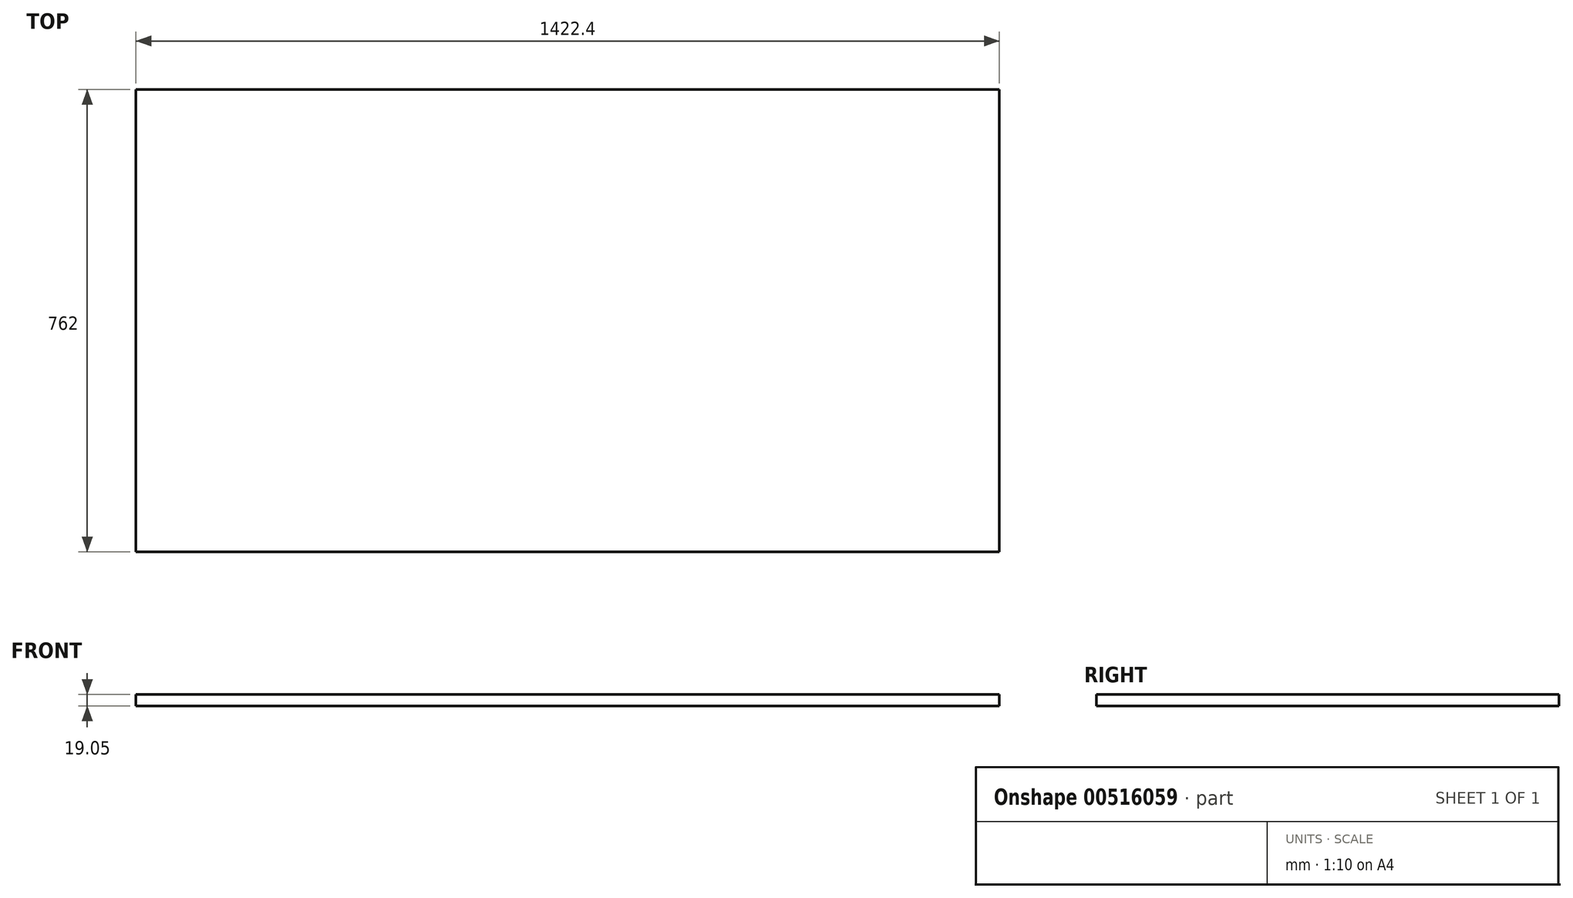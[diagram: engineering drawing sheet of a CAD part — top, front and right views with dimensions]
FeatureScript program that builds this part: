
annotation { "Feature Type Name" : "Feature", "Feature Type Description" : "" }
export const myFeature = defineFeature(function(context is Context, id is Id, definition is map)
    precondition{}
    {
        {
            var Q0;
            Q0=qCreatedBy(makeId("Top.planeOp"),FACE);
            var sketch = newSketch(context, id + "F0", { "sketchPlane" : qUnion([Q0])});
            skLineSegment(sketch, "E0.bottom", {"start": v(711.2, -381) * mm, "end": v(-711.2, -381) * mm});
            skLineSegment(sketch, "E0.top", {"start": v(711.2, 381) * mm, "end": v(-711.2, 381) * mm});
            skLineSegment(sketch, "E0.left", {"start": v(711.2, -381) * mm, "end": v(711.2, 381) * mm});
            skLineSegment(sketch, "E0.right", {"start": v(-711.2, -381) * mm, "end": v(-711.2, 381) * mm});
            skPoint(sketch, "E0.middle", {"position": v(0, 0) * mm});
            skLineSegment(sketch, "E1.bottom", {"start": v(-711.2, -381) * mm, "end": v(1727.2, -381) * mm, "construction": true});
            skLineSegment(sketch, "E1.top", {"start": v(-711.2, 838.2) * mm, "end": v(1727.2, 838.2) * mm, "construction": true});
            skLineSegment(sketch, "E1.left", {"start": v(-711.2, -381) * mm, "end": v(-711.2, 838.2) * mm, "construction": true});
            skLineSegment(sketch, "E1.right", {"start": v(1727.2, -381) * mm, "end": v(1727.2, 838.2) * mm, "construction": true});
            skLineSegment(sketch, "E2.bottom", {"start": v(-711.2, 381) * mm, "end": v(711.2, 381) * mm});
            skLineSegment(sketch, "E3.bottom", {"start": v(1727.2, -381) * mm, "end": v(1066.8, -381) * mm});
            skLineSegment(sketch, "E3.top", {"start": v(1727.2, -76.2) * mm, "end": v(1066.8, -76.2) * mm});
            skLineSegment(sketch, "E3.left", {"start": v(1727.2, -381) * mm, "end": v(1727.2, -76.2) * mm});
            skLineSegment(sketch, "E3.right", {"start": v(1066.8, -381) * mm, "end": v(1066.8, -76.2) * mm});
            skLineSegment(sketch, "E4.top", {"start": v(1727.2, 228.6) * mm, "end": v(1066.8, 228.6) * mm});
            skLineSegment(sketch, "E4.left", {"start": v(1727.2, -76.2) * mm, "end": v(1727.2, 228.6) * mm});
            skLineSegment(sketch, "E4.right", {"start": v(1066.8, -76.2) * mm, "end": v(1066.8, 228.6) * mm});
            skLineSegment(sketch, "E5.top", {"start": v(1727.2, 533.4) * mm, "end": v(1066.8, 533.4) * mm});
            skLineSegment(sketch, "E5.left", {"start": v(1727.2, 228.6) * mm, "end": v(1727.2, 533.4) * mm});
            skLineSegment(sketch, "E5.right", {"start": v(1066.8, 228.6) * mm, "end": v(1066.8, 533.4) * mm});
            skLineSegment(sketch, "E6.top", {"start": v(1727.2, 838.2) * mm, "end": v(1066.8, 838.2) * mm});
            skLineSegment(sketch, "E6.left", {"start": v(1727.2, 533.4) * mm, "end": v(1727.2, 838.2) * mm});
            skLineSegment(sketch, "E6.right", {"start": v(1066.8, 533.4) * mm, "end": v(1066.8, 838.2) * mm});
            skLineSegment(sketch, "E7.bottom", {"start": v(1066.8, -381) * mm, "end": v(762, -381) * mm});
            skLineSegment(sketch, "E7.top", {"start": v(1066.8, 228.6) * mm, "end": v(762, 228.6) * mm});
            skLineSegment(sketch, "E7.left", {"start": v(1066.8, -381) * mm, "end": v(1066.8, 228.6) * mm});
            skLineSegment(sketch, "E7.right", {"start": v(762, -381) * mm, "end": v(762, 228.6) * mm});
            skLineSegment(sketch, "E8.top", {"start": v(1066.8, 838.2) * mm, "end": v(762, 838.2) * mm});
            skLineSegment(sketch, "E8.left", {"start": v(1066.8, 228.6) * mm, "end": v(1066.8, 838.2) * mm});
            skLineSegment(sketch, "E8.right", {"start": v(762, 228.6) * mm, "end": v(762, 838.2) * mm});
            skLineSegment(sketch, "E9", {"start": v(736.6, 838.2) * mm, "end": v(736.6, -381) * mm, "construction": true});
            skLineSegment(sketch, "E10.bottom", {"start": v(-711.2, 838.2) * mm, "end": v(711.2, 838.2) * mm});
            skLineSegment(sketch, "E10.top", {"start": v(-711.2, 533.4) * mm, "end": v(711.2, 533.4) * mm});
            skLineSegment(sketch, "E10.left", {"start": v(-711.2, 838.2) * mm, "end": v(-711.2, 533.4) * mm});
            skLineSegment(sketch, "E10.right", {"start": v(711.2, 838.2) * mm, "end": v(711.2, 533.4) * mm});
            skLineSegment(sketch, "E11", {"start": v(-711.2, 406.4) * mm, "end": v(736.6, 406.4) * mm, "construction": true});
            skSolve(sketch);
        }
        {
            var Q0;
            Q0=makeQuery(id+"F0.imprint","IMPRINT",FACE,{"disambiguationData":[TD([[makeQuery(id+"F0.imprint","IMPRINT",EDGE,{"derivedFrom":sQuery(id+"F0.wireOp",EDGE,"E0.bottom")}),-1.0]])]});
            extrude(context, id + "F1", {"entities" : qUnion([Q0]), "depth" : 19.05 * mm, "offsetDistance" : 25.4 * mm});
        }
    });
